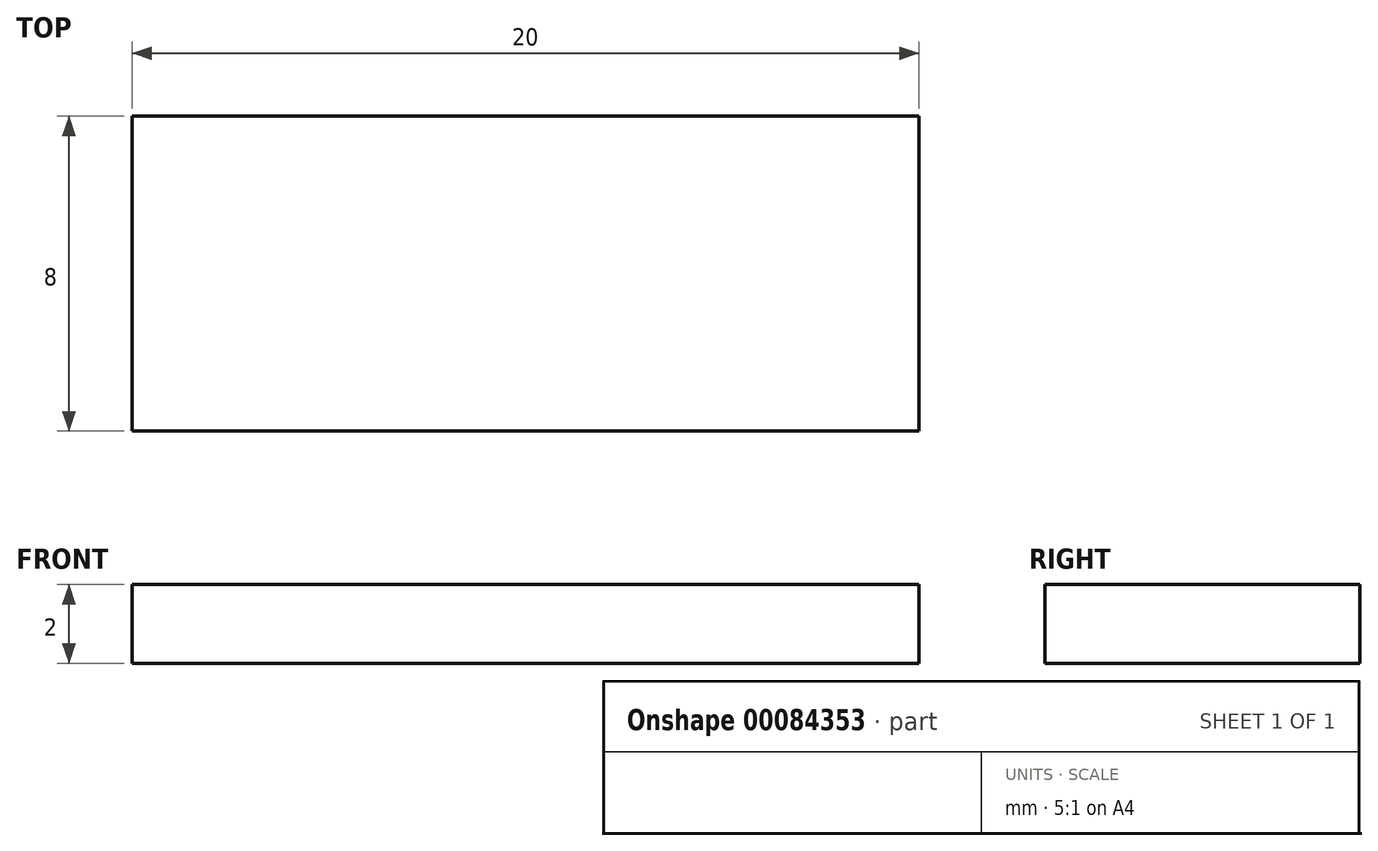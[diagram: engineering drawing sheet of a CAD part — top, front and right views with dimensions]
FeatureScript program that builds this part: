
annotation { "Feature Type Name" : "Feature", "Feature Type Description" : "" }
export const myFeature = defineFeature(function(context is Context, id is Id, definition is map)
    precondition{}
    {
        {
            var Q0;
            Q0=qCreatedBy(makeId("Front.planeOp"),FACE);
            var sketch = newSketch(context, id + "F0", { "sketchPlane" : qUnion([Q0])});
            skLineSegment(sketch, "E0.bottom", {"start": v(0, 0) * mm, "end": v(20, 0) * mm});
            skLineSegment(sketch, "E0.top", {"start": v(0, 2) * mm, "end": v(20, 2) * mm});
            skLineSegment(sketch, "E0.left", {"start": v(0, 0) * mm, "end": v(0, 2) * mm});
            skLineSegment(sketch, "E0.right", {"start": v(20, 0) * mm, "end": v(20, 2) * mm});
            skSolve(sketch);
        }
        {
            var Q0;
            Q0=makeQuery(id+"F0.imprint","IMPRINT",FACE,{"disambiguationData":[TD([[makeQuery(id+"F0.imprint","IMPRINT",EDGE,{"derivedFrom":sQuery(id+"F0.wireOp",EDGE,"E0.bottom")}),1.0]])]});
            extrude(context, id + "F1", {"entities" : qUnion([Q0]), "depth" : 8 * mm});
        }
    });
